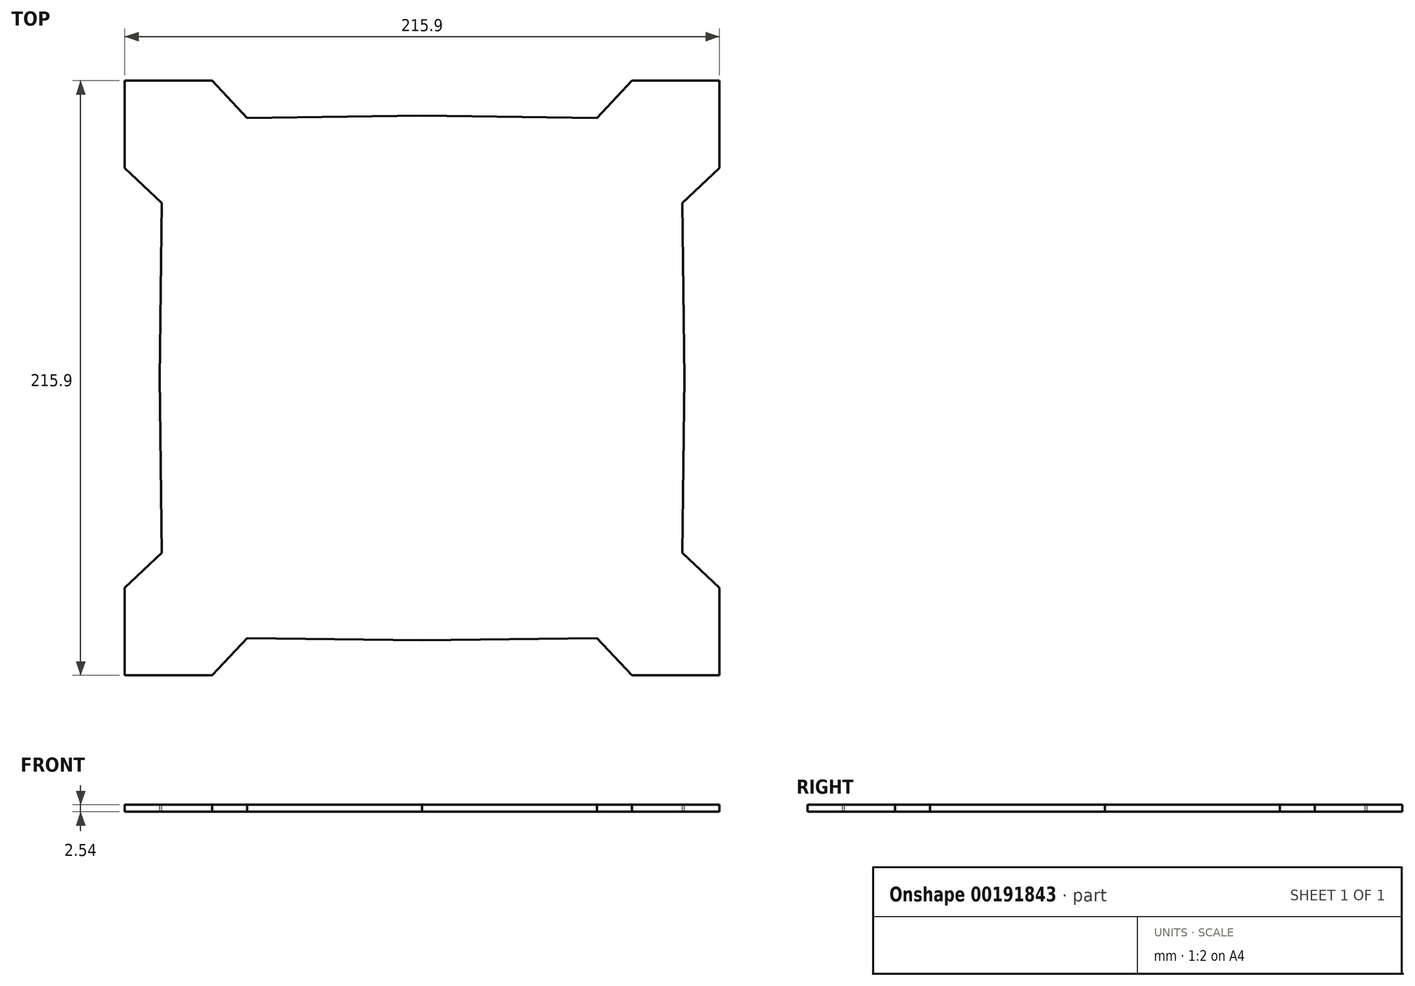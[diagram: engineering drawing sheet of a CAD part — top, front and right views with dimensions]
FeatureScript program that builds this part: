
annotation { "Feature Type Name" : "Feature", "Feature Type Description" : "" }
export const myFeature = defineFeature(function(context is Context, id is Id, definition is map)
    precondition{}
    {
        {
            var Q0;
            Q0=qCreatedBy(makeId("Top.planeOp"),FACE);
            var sketch = newSketch(context, id + "F0", { "sketchPlane" : qUnion([Q0])});
            skLineSegment(sketch, "E0.bottom", {"start": v(107.95, -107.95) * mm, "end": v(-107.95, -107.95) * mm});
            skLineSegment(sketch, "E0.top", {"start": v(107.95, 107.95) * mm, "end": v(-107.95, 107.95) * mm});
            skLineSegment(sketch, "E0.left", {"start": v(107.95, -107.95) * mm, "end": v(107.95, 107.95) * mm});
            skLineSegment(sketch, "E0.right", {"start": v(-107.95, -107.95) * mm, "end": v(-107.95, 107.95) * mm});
            skPoint(sketch, "E0.middle", {"position": v(0, 0) * mm});
            skSolve(sketch);
        }
        {
            var Q0;
            Q0 = qSketchRegion(id + "F0", true);
            extrude(context, id + "F1", {"entities" : qUnion([Q0]), "oppositeDirection" : true, "depth" : 2.54 * mm});
        }
        {
            var Q0;
            Q0=makeQuery(id+"F1.opExtrude","CAP_FACE",FACE,{"disambiguationData":[OSD([sQuery(id+"F0.wireOp",EDGE,"E0.bottom"),sQuery(id+"F0.wireOp",EDGE,"E0.top"),sQuery(id+"F0.wireOp",EDGE,"E0.left"),sQuery(id+"F0.wireOp",EDGE,"E0.right")])],"isStart":true});
            var sketch = newSketch(context, id + "F2", { "sketchPlane" : qUnion([Q0])});
            skLineSegment(sketch, "E1.bottom", {"start": v(0, -107.95) * mm, "end": v(-104.07, -107.95) * mm});
            skPoint(sketch, "E1.middle", {"position": v(0, -101.2) * mm});
            skLineSegment(sketch, "E2.bottom", {"start": v(-53.56, -107.95) * mm, "end": v(-76.2, -107.95) * mm, "construction": true});
            skLineSegment(sketch, "E2.top", {"start": v(-63.5, -94.46) * mm, "end": v(-76.2, -94.46) * mm, "construction": true});
            skLineSegment(sketch, "E2.right", {"start": v(-76.2, -107.95) * mm, "end": v(-76.2, -94.46) * mm, "construction": true});
            skLineSegment(sketch, "E3", {"start": v(-63.5, -94.46) * mm, "end": v(-76.2, -107.95) * mm});
            skLineSegment(sketch, "E4", {"start": v(-104.07, -107.95) * mm, "end": v(-76.2, -107.95) * mm});
            skLineSegment(sketch, "E5", {"start": v(0, -95.25) * mm, "end": v(0, -107.95) * mm});
            skLineSegment(sketch, "E6.trimOffspring", {"start": v(0, -95.25) * mm, "end": v(-63.5, -94.46) * mm});
            skPoint(sketch, "E1.top.end.orphan", {"position": v(63.5, -94.46) * mm});
            skPoint(sketch, "E1.top.start.orphan", {"position": v(104.07, -94.46) * mm});
            skPoint(sketch, "E7.end.orphan", {"position": v(63.5, -107.95) * mm});
            skPoint(sketch, "E7.start.orphan", {"position": v(76.2, -107.95) * mm});
            skSolve(sketch);
        }
        {
            var Q0;
            Q0 = qSketchRegion(id + "F2", true);
            extrude(context, id + "F3", {"entities" : qUnion([Q0]), "endBound" : BoundingType.SYMMETRIC, "oppositeDirection" : true, "depth" : 25.4 * mm});
        }
        {
            var Q0;
            Q0=makeQuery(id+"F3.opExtrude","SWEPT_BODY",BODY,{"disambiguationData":[OSD([sQuery(id+"F2.wireOp",EDGE,"E1.bottom"),sQuery(id+"F2.wireOp",EDGE,"E3"),sQuery(id+"F2.wireOp",EDGE,"E5"),sQuery(id+"F2.wireOp",EDGE,"E6.trimOffspring")])]});
            var Q1;
            Q1=qCreatedBy(makeId("Right.planeOp"),FACE);
            mirror(context, id + "F4", {"entities" : qUnion([Q0]), "mirrorPlane" : qUnion([Q1])});
        }
        {
            var Q0;
            Q0=qCreatedBy(makeId("Front.planeOp"),FACE);
            var sketch = newSketch(context, id + "F5", { "sketchPlane" : qUnion([Q0])});
            skLineSegment(sketch, "E8", {"start": v(0, 0) * mm, "end": v(0, 95.09) * mm});
            skSolve(sketch);
        }
        {
            var Q0;
            Q0=makeQuery(id+"F3.opExtrude","SWEPT_BODY",BODY,{"disambiguationData":[OSD([sQuery(id+"F2.wireOp",EDGE,"E1.bottom"),sQuery(id+"F2.wireOp",EDGE,"E3"),sQuery(id+"F2.wireOp",EDGE,"E5"),sQuery(id+"F2.wireOp",EDGE,"E6.trimOffspring")])]});
            var Q1;
            Q1=makeQuery(id+"F4.opPattern","COPY",BODY,{"derivedFrom":makeQuery(id+"F3.opExtrude","SWEPT_BODY",BODY,{"disambiguationData":[OSD([sQuery(id+"F2.wireOp",EDGE,"E1.bottom"),sQuery(id+"F2.wireOp",EDGE,"E3"),sQuery(id+"F2.wireOp",EDGE,"E5"),sQuery(id+"F2.wireOp",EDGE,"E6.trimOffspring")])]}),"instanceName":"1"});
            var Q2;
            Q2=sQuery(id+"F5.wireOp",EDGE,"E8");
            circularPattern(context, id + "F6", {"entities" : qUnion([Q0, Q1]), "axis" : qUnion([Q2]), "angle" : 90 * degree, "instanceCount" : 4});
        }
        {
            var Q0;
            Q0=makeQuery(id+"F6.opPattern","COPY",FACE,{"derivedFrom":makeQuery(id+"F4.opPattern","COPY",FACE,{"derivedFrom":makeQuery(id+"F3.opExtrude","CAP_FACE",FACE,{"disambiguationData":[OSD([sQuery(id+"F2.wireOp",EDGE,"E1.bottom"),sQuery(id+"F2.wireOp",EDGE,"E3"),sQuery(id+"F2.wireOp",EDGE,"E5"),sQuery(id+"F2.wireOp",EDGE,"E6.trimOffspring")])],"isStart":true}),"instanceName":"1"}),"instanceName":"2"});
            var Q1;
            Q1=makeQuery(id+"F6.opPattern","COPY",FACE,{"derivedFrom":makeQuery(id+"F3.opExtrude","CAP_FACE",FACE,{"disambiguationData":[OSD([sQuery(id+"F2.wireOp",EDGE,"E1.bottom"),sQuery(id+"F2.wireOp",EDGE,"E3"),sQuery(id+"F2.wireOp",EDGE,"E5"),sQuery(id+"F2.wireOp",EDGE,"E6.trimOffspring")])],"isStart":true}),"instanceName":"2"});
            var Q2;
            Q2=makeQuery(id+"F6.opPattern","COPY",FACE,{"derivedFrom":makeQuery(id+"F4.opPattern","COPY",FACE,{"derivedFrom":makeQuery(id+"F3.opExtrude","CAP_FACE",FACE,{"disambiguationData":[OSD([sQuery(id+"F2.wireOp",EDGE,"E1.bottom"),sQuery(id+"F2.wireOp",EDGE,"E3"),sQuery(id+"F2.wireOp",EDGE,"E5"),sQuery(id+"F2.wireOp",EDGE,"E6.trimOffspring")])],"isStart":true}),"instanceName":"1"}),"instanceName":"1"});
            var Q3;
            Q3=makeQuery(id+"F6.opPattern","COPY",FACE,{"derivedFrom":makeQuery(id+"F3.opExtrude","CAP_FACE",FACE,{"disambiguationData":[OSD([sQuery(id+"F2.wireOp",EDGE,"E1.bottom"),sQuery(id+"F2.wireOp",EDGE,"E3"),sQuery(id+"F2.wireOp",EDGE,"E5"),sQuery(id+"F2.wireOp",EDGE,"E6.trimOffspring")])],"isStart":true}),"instanceName":"1"});
            var Q4;
            Q4=makeQuery(id+"F4.opPattern","COPY",FACE,{"derivedFrom":makeQuery(id+"F3.opExtrude","CAP_FACE",FACE,{"disambiguationData":[OSD([sQuery(id+"F2.wireOp",EDGE,"E1.bottom"),sQuery(id+"F2.wireOp",EDGE,"E3"),sQuery(id+"F2.wireOp",EDGE,"E5"),sQuery(id+"F2.wireOp",EDGE,"E6.trimOffspring")])],"isStart":true}),"instanceName":"1"});
            var Q5;
            Q5=makeQuery(id+"F3.opExtrude","CAP_FACE",FACE,{"disambiguationData":[OSD([sQuery(id+"F2.wireOp",EDGE,"E1.bottom"),sQuery(id+"F2.wireOp",EDGE,"E3"),sQuery(id+"F2.wireOp",EDGE,"E5"),sQuery(id+"F2.wireOp",EDGE,"E6.trimOffspring")])],"isStart":true});
            var Q6;
            Q6=makeQuery(id+"F6.opPattern","COPY",FACE,{"derivedFrom":makeQuery(id+"F4.opPattern","COPY",FACE,{"derivedFrom":makeQuery(id+"F3.opExtrude","CAP_FACE",FACE,{"disambiguationData":[OSD([sQuery(id+"F2.wireOp",EDGE,"E1.bottom"),sQuery(id+"F2.wireOp",EDGE,"E3"),sQuery(id+"F2.wireOp",EDGE,"E5"),sQuery(id+"F2.wireOp",EDGE,"E6.trimOffspring")])],"isStart":true}),"instanceName":"1"}),"instanceName":"3"});
            var Q7;
            Q7=makeQuery(id+"F6.opPattern","COPY",FACE,{"derivedFrom":makeQuery(id+"F3.opExtrude","CAP_FACE",FACE,{"disambiguationData":[OSD([sQuery(id+"F2.wireOp",EDGE,"E1.bottom"),sQuery(id+"F2.wireOp",EDGE,"E3"),sQuery(id+"F2.wireOp",EDGE,"E5"),sQuery(id+"F2.wireOp",EDGE,"E6.trimOffspring")])],"isStart":true}),"instanceName":"3"});
            extrude(context, id + "F7", {"entities" : qUnion([Q0, Q1, Q2, Q3, Q4, Q5, Q6, Q7]), "operationType" : NewBodyOperationType.REMOVE, "endBound" : BoundingType.THROUGH_ALL, "oppositeDirection" : true, "depth" : 25.4 * mm});
        }
    });
